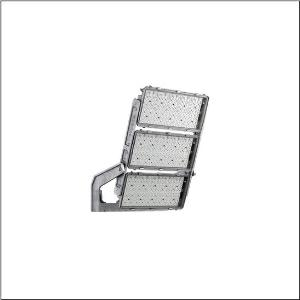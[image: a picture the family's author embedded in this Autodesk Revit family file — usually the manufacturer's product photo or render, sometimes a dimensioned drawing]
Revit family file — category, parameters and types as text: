
# Revit family: floodlight_fl_11_maxi_pro_remote___pl52_5xa779427d01ba_83dd
name_source: partatom
category: Lighting Fixtures
units: mm (PartAtom-declared; Revit-internal decimal feet)

## family parameters
Cut with Voids When Loaded = No
Host = Face
Light Source = No
Part Type = Normal
Room Calculation Point = No
Round Connector Dimension = Use Diameter
Shared = No

## types (1)
- --- (1 x LED, 148130 lm, 1095.9 W, 5000K)
    Apparent Load = 1096 VA
    CIE Flux Codes = 24 55 98 100 100
    Color Rendering = 70
    Color Temperature = 5000K
    Default Elevation = 1800 mm
    Description = Floodlight FL 11  maxi  pro Remote floodlight; light control with lens of PMMA; cover panel of toughened safety glass, transparent; light distribution: PL52, asymmetric direct distribution, LEDcolour temperature: 5000K, rated luminous flux: 148.130lm, colour rendering: CRI > 70, light colour: 750; luminous efficacy: 135lm/W; brightness control: DALI 2 (1 DALI address); with terminal, 8-pole, max. 2.5mm², mains connection: 220..240V/380..400V AC, 50/60Hz, surge voltage resistance: line to ground: 10kV, ECG replaceable separately, LED unit replaceable without ESD environment, dustproof LED module, dimming range 10..100%, no afterglow with DALI off / DMX off command; 1096W floodlight with 3x LED unit of diecast aluminium, coated grey; length: 713mm / width: 651mm / height: 338mm; mounting bracket, of diecast aluminium, uncoated, natural, equipment: Power, protection rating (complete): IP66; insulation class (complete): insulation class I (protective earthing); certification: CE, ENEC, VDE; ball protection: ball impact resistance with accessories, impact resistance: IK07; rated ambient temperature 10°C, only for outdoor installations, permissible operating ambient temperature: -40..+40°C, permissible storage temperature: -40..+85°C; packaging unit: 1 piece

Light Distribution: PL52
    Height = 320 mm
    Lamp = 1 x LED
    Lamp Light Flux = 148130 lm
    Lamp Power = 1095.9 W
    Lamp count = 1
    Length = 1002 mm
    Luminous efficacy = 135 lm/W
    Manufacturer = Siteco
    ModVariant = No
    Model = 5XA779427D01BA
    Mounting Place = Ceiling
    Mounting Type = Surface mounted
    Number of Poles = 1
    OnlyDefault = Yes
    Power Factor = 1
    Product Name = Floodlight FL 11 maxi pro Remote | PL52
    Product group = floodlight | ceiling mounted
    ProductGroupID = 303
    Protection Class = Protection class I
    Protection Degree = IP 66
    RLX_Detail_Level = 1
    RLX_Emergency_Light_Flux = 0 lm
    RLX_Emergency_Type = 0
    RLX_Emergency_Type_DB = No
    RlxData = <blob elided: 52465 chars, md5=0d86dc02>
    Socket = socket
    Standby Power = 0 W
    System Light Flux = 148130 lm
    System Power = 1096 W
    Type Comments = factory setting: luminous flux: 100 % | dim-lin: 254 | 760 mA
    Type Image = l_1006784.jpg
    URL = http://relux.com
    VarID = @adj_046391
    Voltage = 0 V
    Weight = 0.00 kg
    Width = 655 mm

## geometry (parser evidence)
native form markers: Blend x4, Sweep x15
no freeform markers — native parametric forms only
